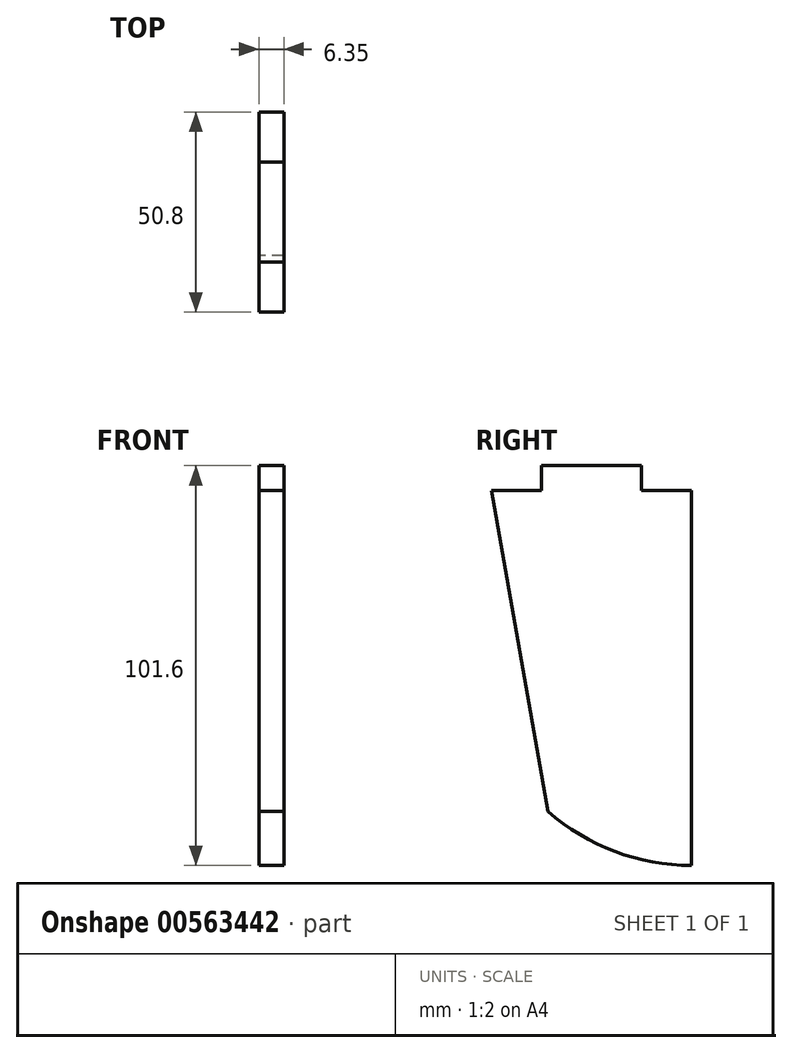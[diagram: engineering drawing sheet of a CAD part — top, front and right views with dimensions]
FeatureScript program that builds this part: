
annotation { "Feature Type Name" : "Feature", "Feature Type Description" : "" }
export const myFeature = defineFeature(function(context is Context, id is Id, definition is map)
    precondition{}
    {
        {
            var Q0;
            Q0=qCreatedBy(makeId("Right.planeOp"),FACE);
            var sketch = newSketch(context, id + "F0", { "sketchPlane" : qUnion([Q0])});
            skLineSegment(sketch, "E0", {"start": v(0, 0) * mm, "end": v(101.6, 0) * mm});
            skLineSegment(sketch, "E1", {"start": v(50.8, 0) * mm, "end": v(50.8, -101.6) * mm});
            skArc(sketch, "E2", {"start": v(50.8, -101.6) * mm, "mid": v(70.26, -98.06) * mm, "end": v(87.22, -87.9) * mm});
            skArc(sketch, "E3.MirrorCS", {"start": v(50.8, -101.6) * mm, "mid": v(31.34, -98.06) * mm, "end": v(14.38, -87.9) * mm});
            skLineSegment(sketch, "E4", {"start": v(101.6, 0) * mm, "end": v(101.6, -6.35) * mm});
            skLineSegment(sketch, "E5", {"start": v(101.6, -6.35) * mm, "end": v(87.22, -87.9) * mm});
            skLineSegment(sketch, "E6.MirrorCS", {"start": v(0, -6.35) * mm, "end": v(14.38, -87.9) * mm});
            skLineSegment(sketch, "E7.MirrorCS", {"start": v(0, 0) * mm, "end": v(0, -6.35) * mm});
            skSolve(sketch);
        }
        {
            var Q0;
            {var subQ2=sQuery(id+"F0.wireOp",EDGE,"E1");Q0=makeQuery(id+"F0.imprint","IMPRINT",FACE,{"disambiguationData":[TD([[makeQuery(id+"F0.imprint","IMPRINT",EDGE,{"derivedFrom":subQ2}),-1.0]])]});}
            var Q1;
            {var subQ0=sQuery(id+"F0.wireOp",EDGE,"khOB3p5o-ioRN-m1G3-Y8gc-wrssJ04mrUhv");Q1=makeQuery(id+"F0.imprint","IMPRINT",FACE,{"disambiguationData":[TD([[makeQuery(id+"F0.imprint","IMPRINT",EDGE,{"derivedFrom":subQ0}),-1.0]])]});}
            var Q2;
            {var subQ1=sQuery(id+"F0.wireOp",EDGE,"E1");Q2=makeQuery(id+"F0.imprint","IMPRINT",FACE,{"disambiguationData":[TD([[makeQuery(id+"F0.imprint","IMPRINT",EDGE,{"derivedFrom":subQ1}),1.0]])]});}
            extrude(context, id + "F1", {"entities" : qUnion([Q0, Q1, Q2]), "depth" : 6.35 * mm, "offsetDistance" : 25.4 * mm});
        }
        {
            var Q0;
            Q0=makeQuery(id+"F1.opExtrude","CAP_FACE",FACE,{"disambiguationData":[OSD([sQuery(id+"F0.wireOp",EDGE,"E0"),sQuery(id+"F0.wireOp",EDGE,"khOB3p5o-ioRN-m1G3-Y8gc-wrssJ04mrUhv"),sQuery(id+"F0.wireOp",EDGE,"E2"),sQuery(id+"F0.wireOp",EDGE,"4d74da0e-6006-49e8-a9db-5cfd90e2330b0.MirrorCS"),sQuery(id+"F0.wireOp",EDGE,"E3.MirrorCS")])],"isStart":false});
            var sketch = newSketch(context, id + "F2", { "sketchPlane" : qUnion([Q0])});
            skLineSegment(sketch, "E8.top", {"start": v(12.7, -6.35) * mm, "end": v(38.1, -6.35) * mm});
            skLineSegment(sketch, "E8.left", {"start": v(12.7, 0) * mm, "end": v(12.7, -6.35) * mm});
            skLineSegment(sketch, "E8.right", {"start": v(38.1, 0) * mm, "end": v(38.1, -6.35) * mm});
            skLineSegment(sketch, "E9", {"start": v(50.8, 0) * mm, "end": v(50.8, -101.6) * mm});
            skLineSegment(sketch, "E10.MirrorCS", {"start": v(63.5, 0) * mm, "end": v(63.5, -6.35) * mm});
            skLineSegment(sketch, "E11.MirrorCS", {"start": v(88.9, 0) * mm, "end": v(88.9, -6.35) * mm});
            skLineSegment(sketch, "E12.MirrorCS", {"start": v(88.9, -6.35) * mm, "end": v(63.5, -6.35) * mm});
            skLineSegment(sketch, "E13", {"start": v(12.7, -6.35) * mm, "end": v(0, -6.35) * mm});
            skLineSegment(sketch, "E14", {"start": v(0, -6.35) * mm, "end": v(0, 0) * mm});
            skLineSegment(sketch, "E15", {"start": v(0, 0) * mm, "end": v(12.7, 0) * mm});
            skLineSegment(sketch, "E16", {"start": v(38.1, -6.35) * mm, "end": v(63.5, -6.35) * mm});
            skLineSegment(sketch, "E17", {"start": v(88.9, -6.35) * mm, "end": v(101.6, -6.35) * mm});
            skLineSegment(sketch, "E18", {"start": v(101.6, -6.35) * mm, "end": v(101.6, 0) * mm});
            skLineSegment(sketch, "E19", {"start": v(101.6, 0) * mm, "end": v(88.9, 0) * mm});
            skLineSegment(sketch, "E20", {"start": v(38.1, 0) * mm, "end": v(63.5, 0) * mm});
            skSolve(sketch);
        }
        {
            var Q0;
            Q0=qSketchRegion(id+"F2",true);
            extrude(context, id + "F3", {"entities" : qUnion([Q0]), "operationType" : NewBodyOperationType.REMOVE, "oppositeDirection" : true, "depth" : 25.4 * mm, "offsetDistance" : 25.4 * mm});
        }
        {
            var Q0;
            Q0=makeQuery(id+"F1.opExtrude","CAP_FACE",FACE,{"disambiguationData":[OSD([sQuery(id+"F0.wireOp",EDGE,"E0"),sQuery(id+"F0.wireOp",EDGE,"E2"),sQuery(id+"F0.wireOp",EDGE,"E3.MirrorCS"),sQuery(id+"F0.wireOp",EDGE,"E4"),sQuery(id+"F0.wireOp",EDGE,"E5"),sQuery(id+"F0.wireOp",EDGE,"E6.MirrorCS"),sQuery(id+"F0.wireOp",EDGE,"E7.MirrorCS")])],"isStart":false});
            var sketch = newSketch(context, id + "F4", { "sketchPlane" : qUnion([Q0])});
            skLineSegment(sketch, "E21", {"start": v(12.32, -76.2) * mm, "end": v(89.28, -76.2) * mm});
            skLineSegment(sketch, "E22", {"start": v(50.8, -6.35) * mm, "end": v(50.8, -101.6) * mm});
            skCircle(sketch, "E23", {"center": v(50.8, -76.2) * mm, "radius": 12.7 * mm});
            skSolve(sketch);
        }
        {
            var Q0;
            {var subQ0=sQuery(id+"F4.wireOp",EDGE,"E23");var subQ1=sQuery(id+"F4.wireOp",EDGE,"E21");var subQ2=makeQuery(id+"F4.imprint","INTERSECT",VERTEX,{"disambiguationData":[OD(0.0)],"derivedFrom":[subQ1,subQ0]});Q0=makeQuery(id+"F4.imprint","IMPRINT",FACE,{"disambiguationData":[TD([[makeQuery(id+"F4.imprint","IMPRINT",EDGE,{"disambiguationData":[TD([[subQ2,-1.0]])],"derivedFrom":subQ1}),-1.0]])]});}
            var Q1;
            {var subQ0=sQuery(id+"F4.wireOp",EDGE,"E22");var subQ1=sQuery(id+"F4.wireOp",EDGE,"E21");var subQ2=makeQuery(id+"F4.imprint","INTERSECT",VERTEX,{"derivedFrom":[subQ1,subQ0]});Q1=makeQuery(id+"F4.imprint","IMPRINT",FACE,{"disambiguationData":[TD([[makeQuery(id+"F4.imprint","IMPRINT",EDGE,{"disambiguationData":[TD([[subQ2,-1.0]])],"derivedFrom":subQ1}),1.0]])]});}
            var Q2;
            {var subQ0=sQuery(id+"F4.wireOp",EDGE,"E22");var subQ1=sQuery(id+"F4.wireOp",EDGE,"E21");var subQ2=makeQuery(id+"F4.imprint","INTERSECT",VERTEX,{"derivedFrom":[subQ1,subQ0]});Q2=makeQuery(id+"F4.imprint","IMPRINT",FACE,{"disambiguationData":[TD([[makeQuery(id+"F4.imprint","IMPRINT",EDGE,{"disambiguationData":[TD([[subQ2,-1.0]])],"derivedFrom":subQ1}),-1.0]])]});}
            var Q3;
            {var subQ0=sQuery(id+"F4.wireOp",EDGE,"E23");var subQ1=sQuery(id+"F4.wireOp",EDGE,"E21");var subQ2=makeQuery(id+"F4.imprint","INTERSECT",VERTEX,{"disambiguationData":[OD(0.0)],"derivedFrom":[subQ1,subQ0]});Q3=makeQuery(id+"F4.imprint","IMPRINT",FACE,{"disambiguationData":[TD([[makeQuery(id+"F4.imprint","IMPRINT",EDGE,{"disambiguationData":[TD([[subQ2,-1.0]])],"derivedFrom":subQ1}),1.0]])]});}
            extrude(context, id + "F5", {"entities" : qUnion([Q0, Q1, Q2, Q3]), "operationType" : NewBodyOperationType.REMOVE, "endBound" : BoundingType.THROUGH_ALL, "oppositeDirection" : true, "depth" : 25.4 * mm, "offsetDistance" : 25.4 * mm});
        }
    });
